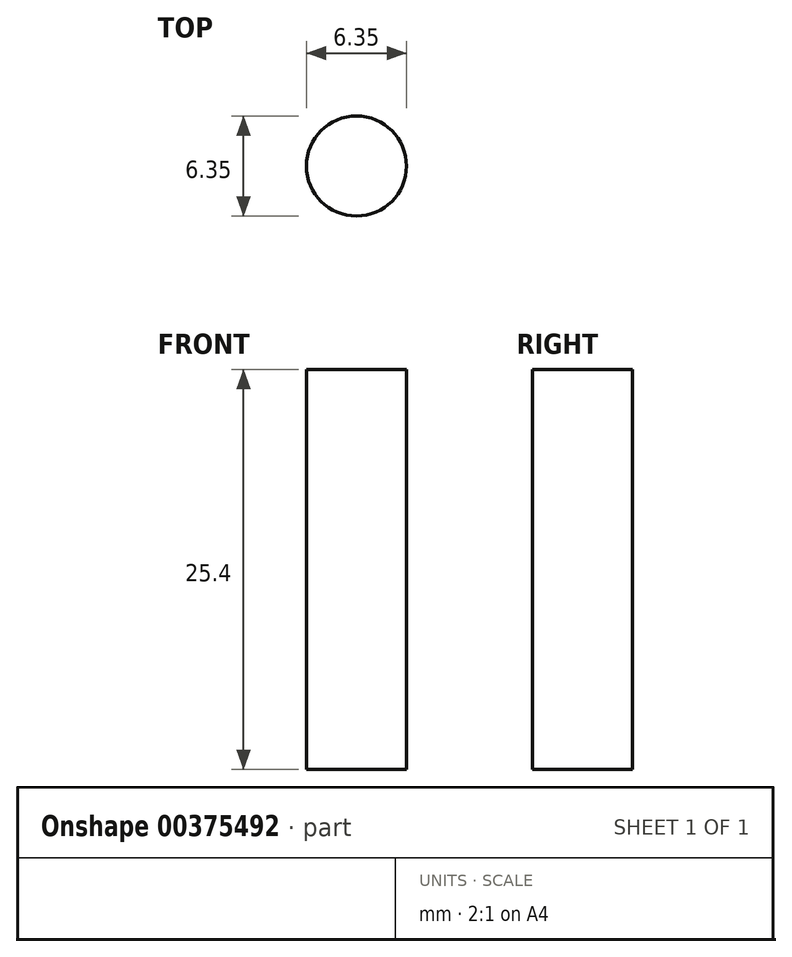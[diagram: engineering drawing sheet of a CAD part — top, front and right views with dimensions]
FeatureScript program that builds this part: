
annotation { "Feature Type Name" : "Feature", "Feature Type Description" : "" }
export const myFeature = defineFeature(function(context is Context, id is Id, definition is map)
    precondition{}
    {
        {
            var Q0;
            Q0=qCreatedBy(makeId("Top.planeOp"),FACE);
            var sketch = newSketch(context, id + "F0", { "sketchPlane" : qUnion([Q0])});
            skCircle(sketch, "E0", {"center": v(-2.42, 2.06) * mm, "radius": 3.18 * mm});
            skSolve(sketch);
        }
        {
            var Q0;
            Q0=makeQuery(id+"F0.imprint","IMPRINT",FACE,{"disambiguationData":[TD([[makeQuery(id+"F0.imprint","IMPRINT",EDGE,{"derivedFrom":sQuery(id+"F0.wireOp",EDGE,"E0")}),1.0]])]});
            extrude(context, id + "F1", {"entities" : qUnion([Q0]), "depth" : 25.4 * mm});
        }
    });
